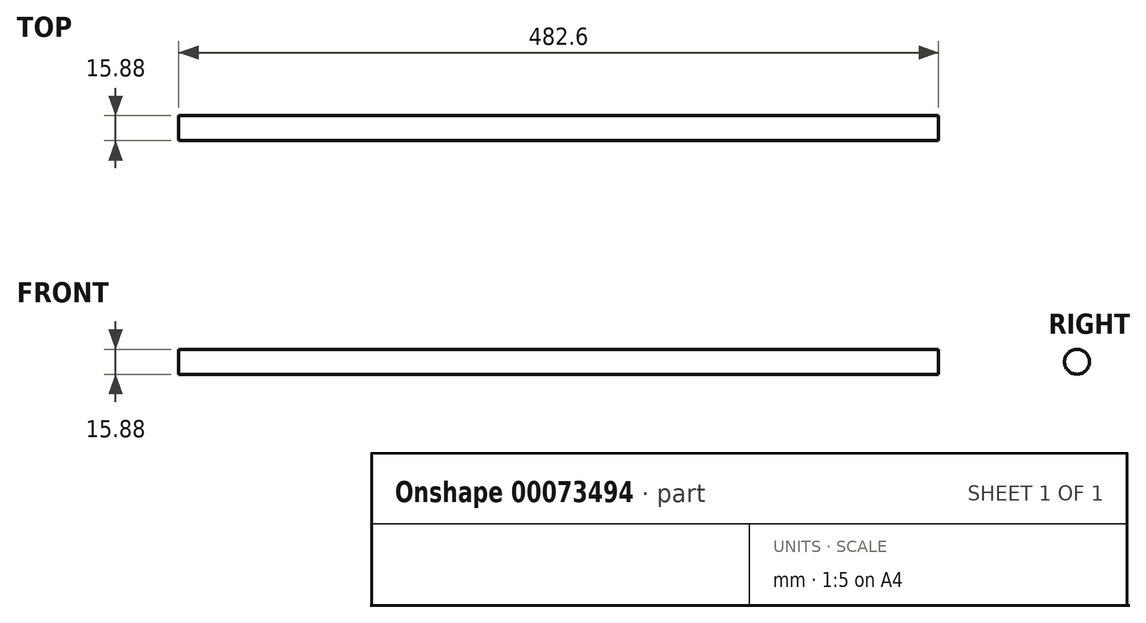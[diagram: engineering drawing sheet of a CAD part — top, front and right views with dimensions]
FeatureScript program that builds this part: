
annotation { "Feature Type Name" : "Feature", "Feature Type Description" : "" }
export const myFeature = defineFeature(function(context is Context, id is Id, definition is map)
    precondition{}
    {
        {
            var Q0;
            Q0=qCreatedBy(makeId("Right.planeOp"),FACE);
            var sketch = newSketch(context, id + "F0", { "sketchPlane" : qUnion([Q0])});
            skCircle(sketch, "E0", {"center": v(0, 0) * mm, "radius": 7.94 * mm});
            skSolve(sketch);
        }
        {
            var Q0;
            Q0=makeQuery(id+"F0.imprint","IMPRINT",FACE,{"disambiguationData":[TD([[makeQuery(id+"F0.imprint","IMPRINT",EDGE,{"derivedFrom":sQuery(id+"F0.wireOp",EDGE,"E0")}),1.0]])]});
            extrude(context, id + "F1", {"entities" : qUnion([Q0]), "depth" : 482.6 * mm});
        }
    });
